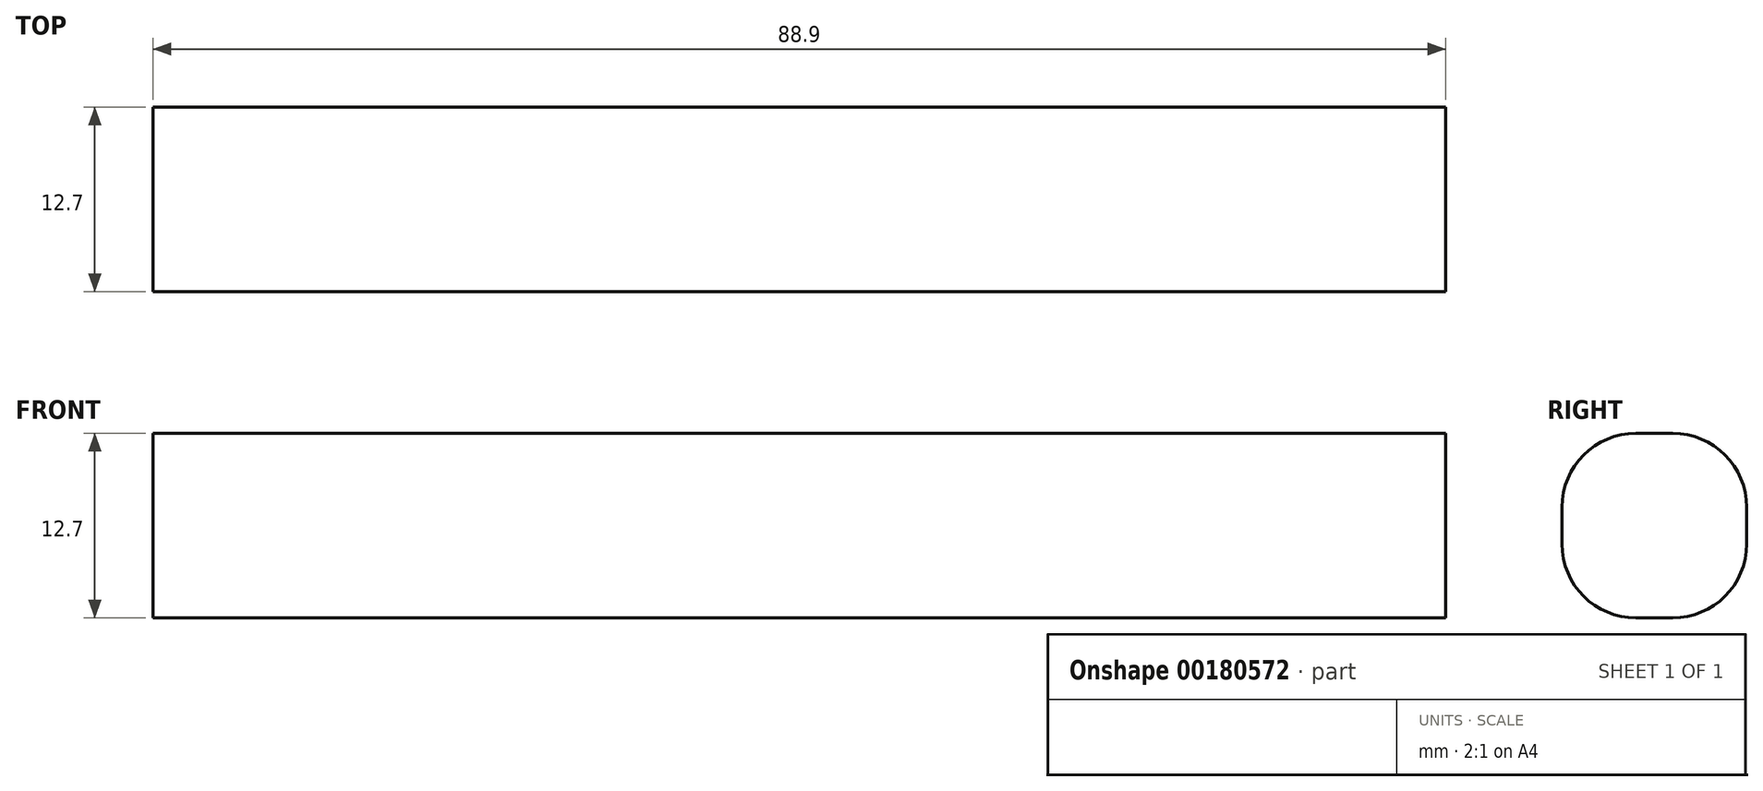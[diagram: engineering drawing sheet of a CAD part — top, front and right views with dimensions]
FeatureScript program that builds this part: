
annotation { "Feature Type Name" : "Feature", "Feature Type Description" : "" }
export const myFeature = defineFeature(function(context is Context, id is Id, definition is map)
    precondition{}
    {
        {
            var Q0;
            Q0=qCreatedBy(makeId("Front.planeOp"),FACE);
            var sketch = newSketch(context, id + "F0", { "sketchPlane" : qUnion([Q0])});
            skPoint(sketch, "E0.middle", {"position": v(0, 0) * mm});
            skLineSegment(sketch, "E1.bottom", {"start": v(44.45, 6.35) * mm, "end": v(-44.45, 6.35) * mm});
            skLineSegment(sketch, "E1.top", {"start": v(44.45, -6.35) * mm, "end": v(-44.45, -6.35) * mm});
            skLineSegment(sketch, "E1.left", {"start": v(44.45, 6.35) * mm, "end": v(44.45, -6.35) * mm});
            skLineSegment(sketch, "E1.right", {"start": v(-44.45, 6.35) * mm, "end": v(-44.45, -6.35) * mm});
            skSolve(sketch);
        }
        {
            var Q0;
            Q0 = qSketchRegion(id + "F0", true);
            extrude(context, id + "F1", {"entities" : qUnion([Q0]), "depth" : 12.7 * mm});
        }
        {
            var Q0;
            Q0=makeQuery(id+"F1.opExtrude","CAP_EDGE",EDGE,{"disambiguationData":[OSD([sQuery(id+"F0.wireOp",EDGE,"E1.bottom")])],"isStart":false});
            var Q1;
            Q1=makeQuery(id+"F1.opExtrude","CAP_EDGE",EDGE,{"disambiguationData":[OSD([sQuery(id+"F0.wireOp",EDGE,"E1.bottom")])],"isStart":true});
            var Q2;
            Q2=makeQuery(id+"F1.opExtrude","CAP_EDGE",EDGE,{"disambiguationData":[OSD([sQuery(id+"F0.wireOp",EDGE,"E1.top")])],"isStart":true});
            var Q3;
            Q3=makeQuery(id+"F1.opExtrude","CAP_EDGE",EDGE,{"disambiguationData":[OSD([sQuery(id+"F0.wireOp",EDGE,"E1.top")])],"isStart":false});
            fillet(context, id + "F2", {"entities" : qUnion([Q0, Q1, Q2, Q3]), "radius" : 5.08 * mm, "tangentPropagation" : true, "allowEdgeOverflow" : false});
        }
    });
